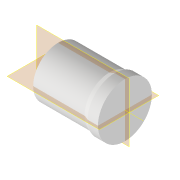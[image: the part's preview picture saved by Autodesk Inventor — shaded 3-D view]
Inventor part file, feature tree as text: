
AUTODESK INVENTOR PART (.ipt)
format: ipt  version: 2022 (Build 260153000, 153)  size: 113,664 bytes
history: native  units: mm
features: plane x2, revolve x1, other x1, sketch x1
ambient origin geometry x8: Origin, YZ Plane, XZ Plane, XY Plane, X Axis, Y Axis, Z Axis, Center Point
bodies: Volumenkörper1 (feature_tree)
feature tree (5):
  revolve  "Umdrehung1"
  plane  "Arbeitsebene1"
  plane  "Arbeitsebene2"
  other  "Arbeitsachse1"
  sketch  "Skizze1"  dims[d0=21.0mm d1=8.0mm d2=52.0mm d3=12.0mm d4=19.5mm d5=0.0mm d6=90.0deg d7=0.0mm d8=0.0mm]
